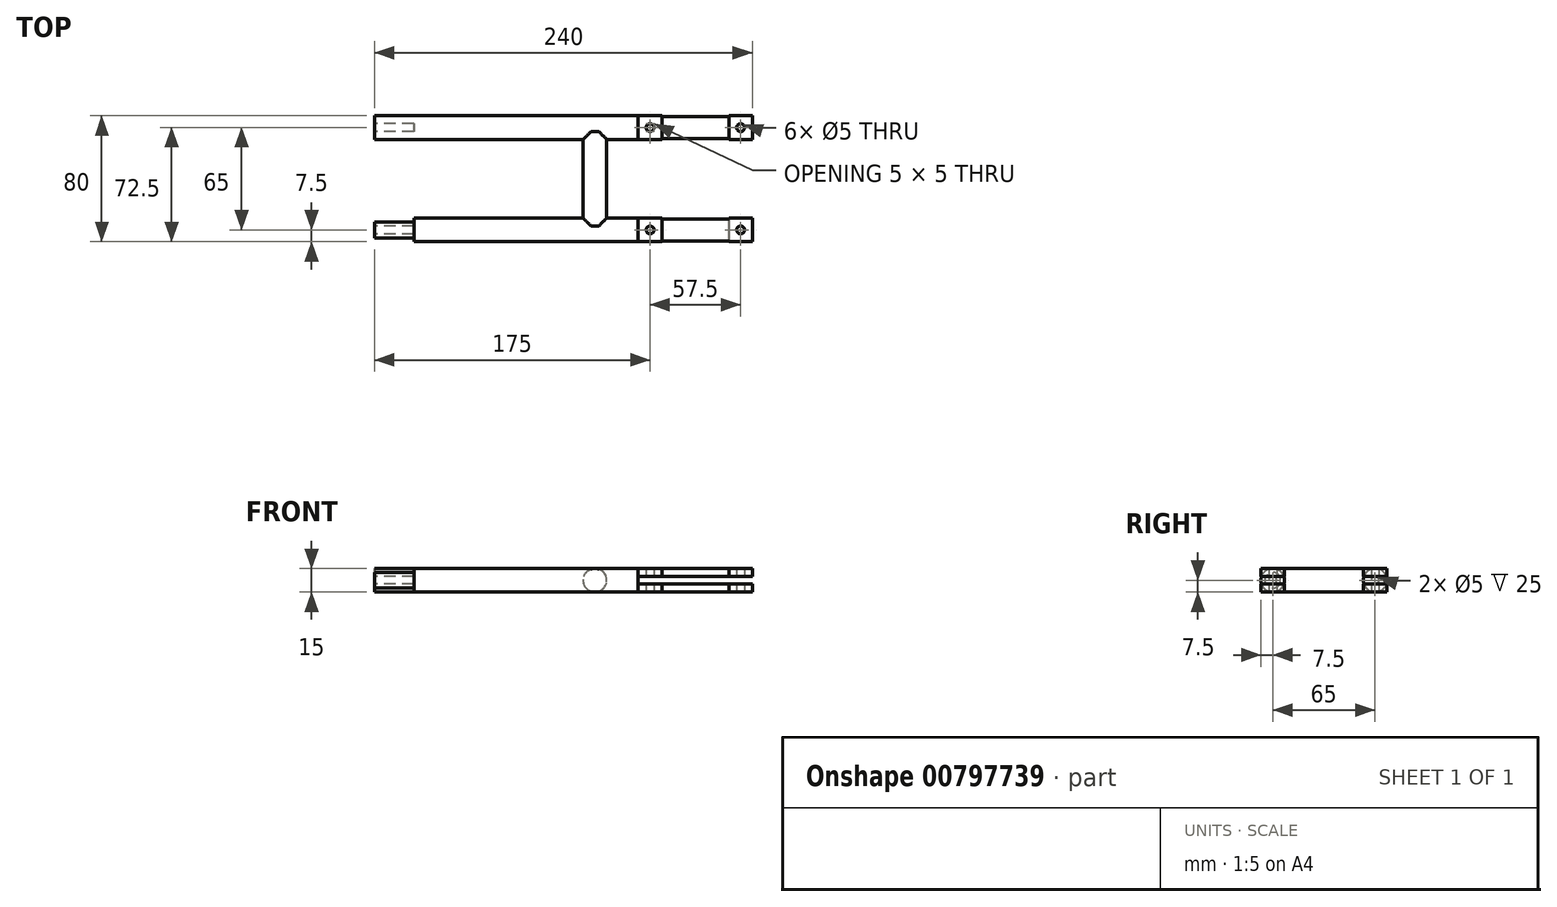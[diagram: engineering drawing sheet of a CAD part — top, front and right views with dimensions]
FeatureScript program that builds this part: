
annotation { "Feature Type Name" : "Feature", "Feature Type Description" : "" }
export const myFeature = defineFeature(function(context is Context, id is Id, definition is map)
    precondition{}
    {
        {
            var Q0;
            Q0=qCreatedBy(makeId("Top.planeOp"),FACE);
            var sketch = newSketch(context, id + "F0", { "sketchPlane" : qUnion([Q0])});
            skLineSegment(sketch, "E0", {"start": v(0, -30) * mm, "end": v(0, 30) * mm, "construction": true});
            skLineSegment(sketch, "E1", {"start": v(0, -30) * mm, "end": v(-240, -30) * mm, "construction": true});
            skLineSegment(sketch, "E2", {"start": v(-240, -30) * mm, "end": v(-240, 30) * mm, "construction": true});
            skLineSegment(sketch, "E3", {"start": v(-240, 30) * mm, "end": v(0, 30) * mm, "construction": true});
            skLineSegment(sketch, "E4.bottom", {"start": v(-240, -40) * mm, "end": v(0, -40) * mm});
            skLineSegment(sketch, "E4.top", {"start": v(-240, -25) * mm, "end": v(-115, -25) * mm});
            skLineSegment(sketch, "E4.left", {"start": v(-240, -40) * mm, "end": v(-240, -25) * mm});
            skPoint(sketch, "E4.middle", {"position": v(0, -30) * mm});
            skLineSegment(sketch, "E5", {"start": v(0, -40) * mm, "end": v(0, -25) * mm});
            skLineSegment(sketch, "E6.MirrorCS", {"start": v(-240, 40) * mm, "end": v(0, 40) * mm});
            skLineSegment(sketch, "E7.MirrorCS", {"start": v(0, 40) * mm, "end": v(0, 25) * mm});
            skLineSegment(sketch, "E8.MirrorCS", {"start": v(-240, 25) * mm, "end": v(-115, 25) * mm});
            skLineSegment(sketch, "E9.MirrorCS", {"start": v(-240, 40) * mm, "end": v(-240, 25) * mm});
            skPoint(sketch, "E10", {"position": v(-50, -30) * mm});
            skPoint(sketch, "E11", {"position": v(-50, 30) * mm});
            skLineSegment(sketch, "E12.left", {"start": v(-100, -25) * mm, "end": v(-100, 25) * mm});
            skLineSegment(sketch, "E12.right", {"start": v(-115, -25) * mm, "end": v(-115, 25) * mm});
            skLineSegment(sketch, "E13.trimOffspring", {"start": v(-100, -25) * mm, "end": v(0, -25) * mm});
            skLineSegment(sketch, "E14.trimOffspring", {"start": v(-100, 25) * mm, "end": v(0, 25) * mm});
            skPoint(sketch, "E15", {"position": v(-100, -30) * mm});
            skPoint(sketch, "E16", {"position": v(-100, 30) * mm});
            skLineSegment(sketch, "E17", {"start": v(-100, -30) * mm, "end": v(-100, 30) * mm, "construction": true});
            skPoint(sketch, "E18", {"position": v(-100, 0) * mm});
            skPoint(sketch, "E19", {"position": v(-240, 0) * mm});
            skPoint(sketch, "E20", {"position": v(-220, 0) * mm});
            skLineSegment(sketch, "E21", {"start": v(-240, 0) * mm, "end": v(-220, 0) * mm, "construction": true});
            skLineSegment(sketch, "E22", {"start": v(-115, 0) * mm, "end": v(-220, 0) * mm, "construction": true});
            skPoint(sketch, "E23", {"position": v(-130, 0) * mm});
            skSolve(sketch);
        }
        {
            var Q0;
            Q0=makeQuery(id+"F0.imprint","IMPRINT",FACE,{"disambiguationData":[TD([[makeQuery(id+"F0.imprint","IMPRINT",EDGE,{"derivedFrom":sQuery(id+"F0.wireOp",EDGE,"E4.bottom")}),1.0]])]});
            extrude(context, id + "F1", {"entities" : qUnion([Q0]), "depth" : 15 * mm, "offsetDistance" : 25 * mm});
        }
        {
            var Q0;
            Q0=qCreatedBy(makeId("Right.planeOp"),FACE);
            var sketch = newSketch(context, id + "F2", { "sketchPlane" : qUnion([Q0])});
            skLineSegment(sketch, "E24", {"start": v(0, 0) * mm, "end": v(0, 7.5) * mm, "construction": true});
            skLineSegment(sketch, "E25", {"start": v(-40, 7.5) * mm, "end": v(40, 7.5) * mm, "construction": true});
            skPoint(sketch, "E26", {"position": v(-32.5, 7.5) * mm});
            skPoint(sketch, "E27", {"position": v(32.5, 7.5) * mm});
            skCircle(sketch, "E28", {"center": v(-32.5, 7.5) * mm, "radius": 7.5 * mm});
            skCircle(sketch, "E29", {"center": v(32.5, 7.5) * mm, "radius": 7.5 * mm});
            skSolve(sketch);
        }
        {
            var Q0;
            Q0 = qSketchRegion(id + "F2", true);
            extrude(context, id + "F3", {"entities" : qUnion([Q0]), "operationType" : NewBodyOperationType.INTERSECT, "oppositeDirection" : true, "depth" : 240 * mm, "offsetDistance" : 25 * mm});
        }
        {
            var Q0;
            Q0=qCreatedBy(makeId("Front.planeOp"),FACE);
            var sketch = newSketch(context, id + "F4", { "sketchPlane" : qUnion([Q0])});
            skLineSegment(sketch, "E30", {"start": v(0, 0) * mm, "end": v(0, 7.5) * mm, "construction": true});
            skLineSegment(sketch, "E31", {"start": v(0, 7.5) * mm, "end": v(-100, 7.5) * mm, "construction": true});
            skCircle(sketch, "E32", {"center": v(-100, 7.5) * mm, "radius": 7.5 * mm});
            skSolve(sketch);
        }
        {
            var Q0;
            Q0 = qSketchRegion(id + "F4", true);
            var Q1;
            Q1 = qSketchRegion(id + "F6", true);
            extrude(context, id + "F5", {"entities" : qUnion([Q0, Q1]), "operationType" : NewBodyOperationType.ADD, "depth" : 30 * mm, "offsetDistance" : 25 * mm, "hasSecondDirection" : true, "secondDirectionOppositeDirection" : true, "secondDirectionDepth" : 30 * mm});
        }
        {
            var Q0;
            Q0=qCreatedBy(makeId("Top.planeOp"),FACE);
            var sketch = newSketch(context, id + "F6", { "sketchPlane" : qUnion([Q0])});
            skLineSegment(sketch, "E33", {"start": v(0, 0) * mm, "end": v(0, 40) * mm, "construction": true});
            skLineSegment(sketch, "E34", {"start": v(0, 40) * mm, "end": v(-72.5, 40) * mm, "construction": true});
            skLineSegment(sketch, "E35", {"start": v(-72.5, 40) * mm, "end": v(-72.5, -40) * mm, "construction": true});
            skLineSegment(sketch, "E36", {"start": v(-72.5, -40) * mm, "end": v(0, -40) * mm, "construction": true});
            skLineSegment(sketch, "E37", {"start": v(0, -40) * mm, "end": v(0, 0) * mm, "construction": true});
            skPoint(sketch, "E38", {"position": v(-72.5, 25) * mm});
            skPoint(sketch, "E39", {"position": v(-72.5, -25) * mm});
            skPoint(sketch, "E40", {"position": v(0, -25) * mm});
            skPoint(sketch, "E41", {"position": v(0, 25) * mm});
            skPoint(sketch, "E42", {"position": v(-57.5, 40) * mm});
            skPoint(sketch, "E43", {"position": v(-57.5, -40) * mm});
            skPoint(sketch, "E44", {"position": v(-15, 40) * mm});
            skPoint(sketch, "E45", {"position": v(-15, -40) * mm});
            skLineSegment(sketch, "E46", {"start": v(-72.5, 40) * mm, "end": v(-57.5, 40) * mm});
            skLineSegment(sketch, "E47", {"start": v(-57.5, 25) * mm, "end": v(-72.5, 25) * mm});
            skLineSegment(sketch, "E48", {"start": v(-57.5, 25) * mm, "end": v(-57.5, 40) * mm});
            skLineSegment(sketch, "E49", {"start": v(-72.5, -25) * mm, "end": v(-57.5, -25) * mm});
            skLineSegment(sketch, "E50", {"start": v(-57.5, -40) * mm, "end": v(-57.5, -25) * mm});
            skLineSegment(sketch, "E51", {"start": v(-57.5, -40) * mm, "end": v(-72.5, -40) * mm});
            skLineSegment(sketch, "E52", {"start": v(-72.5, -40) * mm, "end": v(-72.5, -25) * mm});
            skLineSegment(sketch, "E53", {"start": v(-72.5, 25) * mm, "end": v(-72.5, 40) * mm});
            skLineSegment(sketch, "E54", {"start": v(0, 40) * mm, "end": v(-15, 40) * mm});
            skLineSegment(sketch, "E55", {"start": v(-15, 40) * mm, "end": v(-15, 25) * mm});
            skLineSegment(sketch, "E56", {"start": v(0, 25) * mm, "end": v(-15, 25) * mm});
            skLineSegment(sketch, "E57", {"start": v(0, 25) * mm, "end": v(0, 40) * mm});
            skLineSegment(sketch, "E58", {"start": v(0, -25) * mm, "end": v(0, -40) * mm});
            skLineSegment(sketch, "E59", {"start": v(0, -40) * mm, "end": v(-15, -40) * mm});
            skLineSegment(sketch, "E60", {"start": v(-15, -40) * mm, "end": v(-15, -25) * mm});
            skLineSegment(sketch, "E61", {"start": v(0, -25) * mm, "end": v(-15, -25) * mm});
            skSolve(sketch);
        }
        {
            var Q0;
            Q0 = qSketchRegion(id + "F6", true);
            extrude(context, id + "F7", {"entities" : qUnion([Q0]), "operationType" : NewBodyOperationType.ADD, "depth" : 15 * mm, "offsetDistance" : 25 * mm});
        }
        {
            var Q0;
            Q0=qCreatedBy(makeId("Front.planeOp"),FACE);
            var sketch = newSketch(context, id + "F8", { "sketchPlane" : qUnion([Q0])});
            skLineSegment(sketch, "E62", {"start": v(0, 0) * mm, "end": v(0, 10) * mm, "construction": true});
            skLineSegment(sketch, "E63", {"start": v(0, 10) * mm, "end": v(-72.5, 10) * mm, "construction": true});
            skLineSegment(sketch, "E64", {"start": v(-72.5, 10) * mm, "end": v(-72.5, 5) * mm, "construction": true});
            skLineSegment(sketch, "E65", {"start": v(-72.5, 5) * mm, "end": v(-57.5, 5) * mm, "construction": true});
            skLineSegment(sketch, "E66", {"start": v(-57.5, 5) * mm, "end": v(-57.5, 0) * mm, "construction": true});
            skLineSegment(sketch, "E67", {"start": v(-57.5, 0) * mm, "end": v(0, 0) * mm, "construction": true});
            skLineSegment(sketch, "E68", {"start": v(-72.5, 5) * mm, "end": v(-72.5, -2.5) * mm, "construction": true});
            skLineSegment(sketch, "E69", {"start": v(0, 10) * mm, "end": v(0, 0) * mm});
            skLineSegment(sketch, "E70", {"start": v(0, 0) * mm, "end": v(0, 7.5) * mm, "construction": true});
            skLineSegment(sketch, "E71", {"start": v(0, 7.5) * mm, "end": v(-7.5, 7.5) * mm, "construction": true});
            skLineSegment(sketch, "E72", {"start": v(-57.5, 0) * mm, "end": v(0, 0) * mm});
            skLineSegment(sketch, "E73", {"start": v(-72.5, 10) * mm, "end": v(0, 10) * mm});
            skLineSegment(sketch, "E74", {"start": v(-72.5, 5) * mm, "end": v(-57.5, 5) * mm});
            skLineSegment(sketch, "E75", {"start": v(-57.5, 5) * mm, "end": v(-57.5, 0) * mm});
            skLineSegment(sketch, "E76", {"start": v(-72.5, 10) * mm, "end": v(-72.5, 5) * mm});
            skSolve(sketch);
        }
        {
            var Q0;
            Q0 = qSketchRegion(id + "F8", true);
            extrude(context, id + "F9", {"entities" : qUnion([Q0]), "operationType" : NewBodyOperationType.REMOVE, "oppositeDirection" : true, "depth" : 40.1 * mm, "offsetDistance" : 25 * mm});
        }
        {
            var Q0;
            Q0=qCreatedBy(makeId("Front.planeOp"),FACE);
            var sketch = newSketch(context, id + "F10", { "sketchPlane" : qUnion([Q0])});
            skLineSegment(sketch, "E77", {"start": v(0, 0) * mm, "end": v(0, 5) * mm, "construction": true});
            skLineSegment(sketch, "E78", {"start": v(0, 5) * mm, "end": v(0, 10) * mm, "construction": true});
            skLineSegment(sketch, "E79", {"start": v(0, 10) * mm, "end": v(0, 15) * mm, "construction": true});
            skLineSegment(sketch, "E80", {"start": v(0, 15) * mm, "end": v(-57.5, 15) * mm});
            skLineSegment(sketch, "E81", {"start": v(-57.5, 15) * mm, "end": v(-57.5, 10) * mm});
            skLineSegment(sketch, "E82", {"start": v(-57.5, 10) * mm, "end": v(-72.5, 10) * mm});
            skLineSegment(sketch, "E83", {"start": v(-72.5, 10) * mm, "end": v(-72.5, 5) * mm});
            skLineSegment(sketch, "E84", {"start": v(-72.5, 5) * mm, "end": v(-57.5, 5) * mm});
            skLineSegment(sketch, "E85", {"start": v(-57.5, 5) * mm, "end": v(0, 5) * mm});
            skLineSegment(sketch, "E86", {"start": v(0, 5) * mm, "end": v(0, 15) * mm});
            skSolve(sketch);
        }
        {
            var Q0;
            Q0=makeQuery(id+"F10.imprint","IMPRINT",FACE,{"disambiguationData":[TD([[makeQuery(id+"F10.imprint","IMPRINT",EDGE,{"derivedFrom":sQuery(id+"F10.wireOp",EDGE,"E80")}),1.0]])]});
            extrude(context, id + "F11", {"entities" : qUnion([Q0]), "operationType" : NewBodyOperationType.REMOVE, "depth" : 54.1 * mm, "offsetDistance" : 25 * mm});
        }
        {
            var Q0;
            Q0=qCreatedBy(makeId("Top.planeOp"),FACE);
            var sketch = newSketch(context, id + "F12", { "sketchPlane" : qUnion([Q0])});
            skLineSegment(sketch, "E87", {"start": v(0, -40) * mm, "end": v(0, 40) * mm, "construction": true});
            skPoint(sketch, "E88", {"position": v(0, -32.5) * mm});
            skPoint(sketch, "E89", {"position": v(0, 32.5) * mm});
            skLineSegment(sketch, "E90", {"start": v(0, -32.5) * mm, "end": v(-65, -32.5) * mm, "construction": true});
            skLineSegment(sketch, "E91", {"start": v(0, 32.5) * mm, "end": v(-65, 32.5) * mm, "construction": true});
            skPoint(sketch, "E92", {"position": v(-7.5, 32.5) * mm});
            skPoint(sketch, "E93", {"position": v(-7.5, -32.5) * mm});
            skCircle(sketch, "E94", {"center": v(-65, 32.5) * mm, "radius": 2.5 * mm});
            skCircle(sketch, "E95", {"center": v(-65, -32.5) * mm, "radius": 2.5 * mm});
            skCircle(sketch, "E96", {"center": v(-7.5, -32.5) * mm, "radius": 2.5 * mm});
            skCircle(sketch, "E97", {"center": v(-7.5, 32.5) * mm, "radius": 2.5 * mm});
            skSolve(sketch);
        }
        {
            var Q0;
            Q0 = qSketchRegion(id + "F12", true);
            extrude(context, id + "F13", {"entities" : qUnion([Q0]), "operationType" : NewBodyOperationType.REMOVE, "depth" : 25 * mm, "offsetDistance" : 25 * mm});
        }
        {
            var Q0;
            Q0=makeQuery(id+"F1.opExtrude","SWEPT_FACE",FACE,{"disambiguationData":[OSD([sQuery(id+"F0.wireOp",EDGE,"E4.left")])]});
            cPlane(context, id + "F14", {"entities" : qUnion([Q0]), "cplaneType" : CPlaneType.OFFSET, "offset" : 0 * mm, "width" : 150 * mm, "height" : 150 * mm});
        }
        {
            var Q0;
            Q0=qCreatedBy(id+"F14.planeOp",FACE);
            var sketch = newSketch(context, id + "F15", { "sketchPlane" : qUnion([Q0])});
            skLineSegment(sketch, "E98", {"start": v(0, 0) * mm, "end": v(0, 7.5) * mm, "construction": true});
            skLineSegment(sketch, "E99", {"start": v(-32.5, 7.5) * mm, "end": v(32.5, 7.5) * mm, "construction": true});
            skCircle(sketch, "E100", {"center": v(32.5, 7.5) * mm, "radius": 2.5 * mm});
            skCircle(sketch, "E101", {"center": v(-32.5, 7.5) * mm, "radius": 2.5 * mm});
            skCircle(sketch, "E102", {"center": v(-32.5, 7.5) * mm, "radius": 5 * mm});
            skCircle(sketch, "E103", {"center": v(32.5, 7.5) * mm, "radius": 5 * mm});
            skSolve(sketch);
        }
        {
            var Q0;
            Q0=makeQuery(id+"F15.imprint","IMPRINT",FACE,{"disambiguationData":[TD([[makeQuery(id+"F15.imprint","IMPRINT",EDGE,{"derivedFrom":sQuery(id+"F15.wireOp",EDGE,"E101")}),1.0]])]});
            var Q1;
            Q1=makeQuery(id+"F15.imprint","IMPRINT",FACE,{"disambiguationData":[TD([[makeQuery(id+"F15.imprint","IMPRINT",EDGE,{"derivedFrom":sQuery(id+"F15.wireOp",EDGE,"E100")}),1.0]])]});
            extrude(context, id + "F16", {"entities" : qUnion([Q0, Q1]), "operationType" : NewBodyOperationType.REMOVE, "oppositeDirection" : true, "depth" : 25 * mm, "offsetDistance" : 25 * mm});
        }
        {
            var Q0;
            Q0=qCreatedBy(id+"F14.planeOp",FACE);
            var sketch = newSketch(context, id + "F17", { "sketchPlane" : qUnion([Q0])});
            skLineSegment(sketch, "E104", {"start": v(0, 0) * mm, "end": v(0, 7.5) * mm, "construction": true});
            skLineSegment(sketch, "E105", {"start": v(32.5, 7.5) * mm, "end": v(-32.5, 7.5) * mm, "construction": true});
            skCircle(sketch, "E106", {"center": v(32.5, 7.5) * mm, "radius": 5 * mm});
            skCircle(sketch, "E107", {"center": v(32.5, 7.5) * mm, "radius": 7.5 * mm});
            skCircle(sketch, "E108.MirrorC", {"center": v(-32.5, 7.5) * mm, "radius": 7.5 * mm});
            skCircle(sketch, "E109.MirrorC", {"center": v(-32.5, 7.5) * mm, "radius": 5 * mm});
            skSolve(sketch);
        }
        {
            var Q0;
            Q0 = qSketchRegion(id + "F0", true);
            extrude(context, id + "F18", {"entities" : qUnion([Q0]), "operationType" : NewBodyOperationType.REMOVE, "oppositeDirection" : true, "depth" : 25 * mm, "offsetDistance" : 25 * mm});
        }
        {
            var Q0;
            Q0=makeQuery(id+"F17.imprint","IMPRINT",FACE,{"disambiguationData":[TD([[makeQuery(id+"F17.imprint","IMPRINT",EDGE,{"derivedFrom":sQuery(id+"F17.wireOp",EDGE,"E108.MirrorC")}),-1.0]])]});
            var Q1;
            Q1=makeQuery(id+"F17.imprint","IMPRINT",FACE,{"disambiguationData":[TD([[makeQuery(id+"F17.imprint","IMPRINT",EDGE,{"derivedFrom":sQuery(id+"F17.wireOp",EDGE,"E106")}),-1.0]])]});
            extrude(context, id + "F19", {"entities" : qUnion([Q0, Q1]), "operationType" : NewBodyOperationType.REMOVE, "oppositeDirection" : true, "depth" : 25 * mm, "offsetDistance" : 25 * mm});
        }
    });
